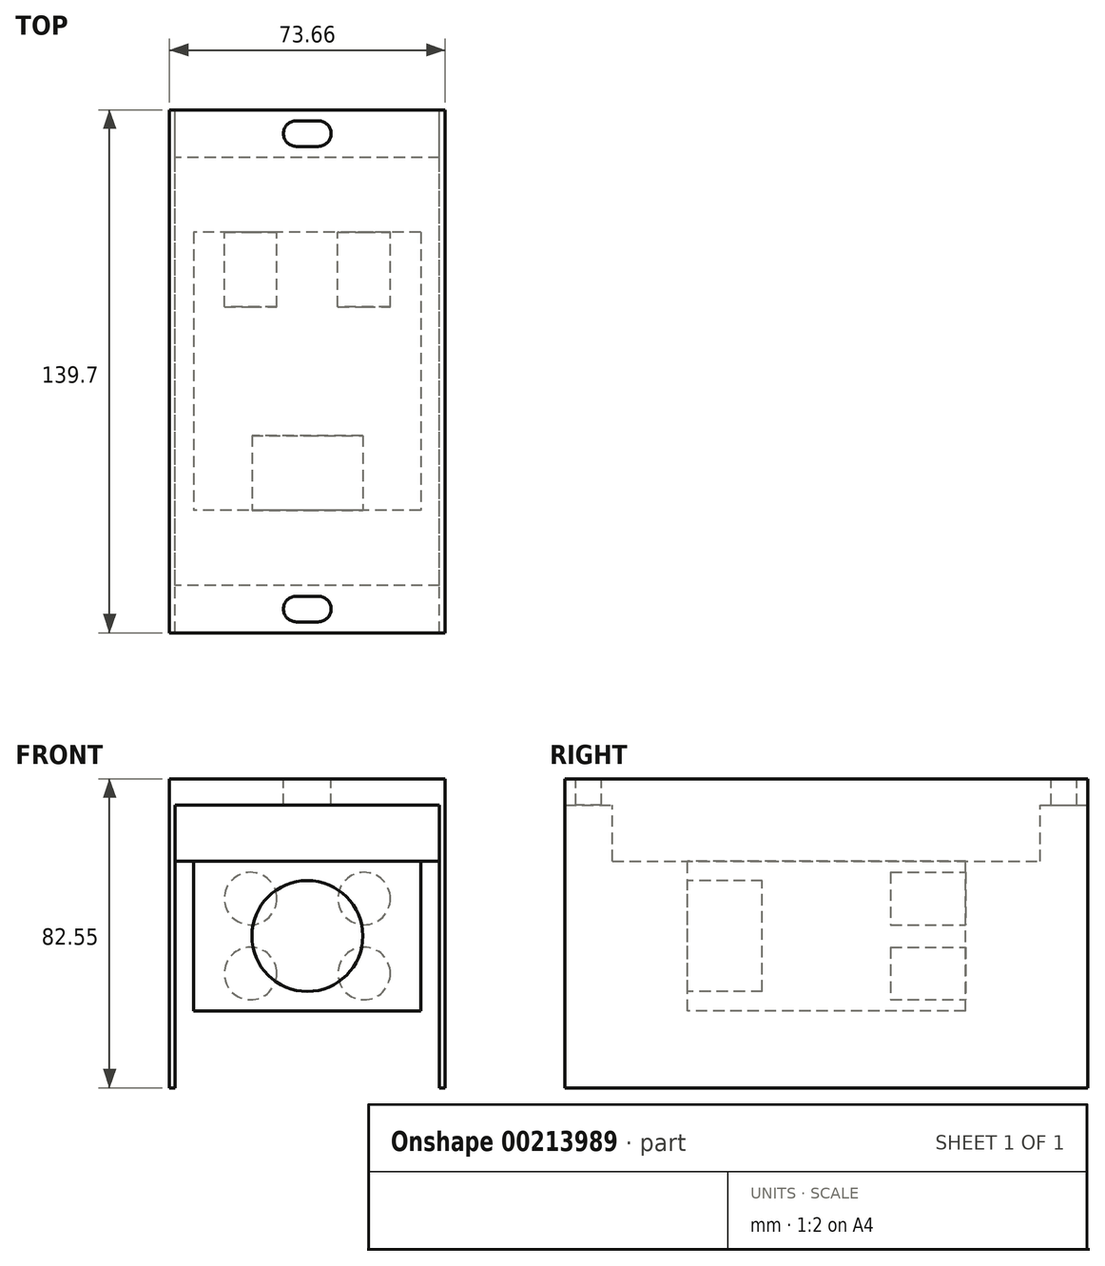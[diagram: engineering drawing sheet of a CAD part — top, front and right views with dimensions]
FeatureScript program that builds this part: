
annotation { "Feature Type Name" : "Feature", "Feature Type Description" : "" }
export const myFeature = defineFeature(function(context is Context, id is Id, definition is map)
    precondition{}
    {
        {
            var Q0;
            Q0=qCreatedBy(makeId("Top.planeOp"),FACE);
            var sketch = newSketch(context, id + "F0", { "sketchPlane" : qUnion([Q0])});
            skLineSegment(sketch, "E0.bottom", {"start": v(-36.83, 69.85) * mm, "end": v(36.83, 69.85) * mm});
            skLineSegment(sketch, "E0.top", {"start": v(-36.83, -69.85) * mm, "end": v(36.83, -69.85) * mm});
            skLineSegment(sketch, "E0.left", {"start": v(-36.83, 69.85) * mm, "end": v(-36.83, -69.85) * mm});
            skLineSegment(sketch, "E0.right", {"start": v(36.83, 69.85) * mm, "end": v(36.83, -69.85) * mm});
            skPoint(sketch, "E0.middle", {"position": v(0, 0) * mm});
            skCircle(sketch, "E1", {"center": v(2.92, 63.5) * mm, "radius": 3.43 * mm});
            skCircle(sketch, "E2", {"center": v(-2.92, 63.5) * mm, "radius": 3.43 * mm});
            skLineSegment(sketch, "E3", {"start": v(0, 69.85) * mm, "end": v(0, -69.85) * mm, "construction": true});
            skLineSegment(sketch, "E4", {"start": v(2.92, 66.93) * mm, "end": v(-2.92, 66.93) * mm});
            skLineSegment(sketch, "E5", {"start": v(-2.92, 60.07) * mm, "end": v(2.92, 60.07) * mm});
            skLineSegment(sketch, "E6", {"start": v(36.83, 0) * mm, "end": v(-36.83, 0) * mm, "construction": true});
            skLineSegment(sketch, "E7.MirrorCS", {"start": v(-2.92, -60.07) * mm, "end": v(2.92, -60.07) * mm});
            skCircle(sketch, "E8.MirrorC", {"center": v(-2.92, -63.5) * mm, "radius": 3.43 * mm});
            skLineSegment(sketch, "E9.MirrorCS", {"start": v(2.92, -66.93) * mm, "end": v(-2.92, -66.93) * mm});
            skCircle(sketch, "E10.MirrorC", {"center": v(2.92, -63.5) * mm, "radius": 3.43 * mm});
            skLineSegment(sketch, "E11", {"start": v(35.33, -69.85) * mm, "end": v(35.33, 69.85) * mm});
            skLineSegment(sketch, "E12.MirrorCS", {"start": v(-35.33, -69.85) * mm, "end": v(-35.33, 69.85) * mm});
            skLineSegment(sketch, "E13", {"start": v(35.33, 57.15) * mm, "end": v(-35.33, 57.15) * mm});
            skLineSegment(sketch, "E14.MirrorCS", {"start": v(35.33, -57.15) * mm, "end": v(-35.33, -57.15) * mm});
            skLineSegment(sketch, "E15", {"start": v(0, 57.15) * mm, "end": v(0, 69.85) * mm, "construction": true});
            skPoint(sketch, "E16", {"position": v(0, 63.5) * mm});
            skSolve(sketch);
        }
        {
            var Q0;
            {var subQ0=sQuery(id+"F0.wireOp",EDGE,"E13");Q0=makeQuery(id+"F0.imprint","IMPRINT",FACE,{"disambiguationData":[TD([[makeQuery(id+"F0.imprint","IMPRINT",EDGE,{"derivedFrom":subQ0}),1.0]])]});}
            extrude(context, id + "F1", {"entities" : qUnion([Q0]), "oppositeDirection" : true, "depth" : 22 * mm});
        }
        {
            var Q0;
            {var subQ2=sQuery(id+"F0.wireOp",EDGE,"E7.MirrorCS");Q0=makeQuery(id+"F0.imprint","IMPRINT",FACE,{"disambiguationData":[TD([[makeQuery(id+"F0.imprint","IMPRINT",EDGE,{"derivedFrom":subQ2}),1.0]])]});}
            var Q1;
            {var subQ0=sQuery(id+"F0.wireOp",EDGE,"E4");Q1=makeQuery(id+"F0.imprint","IMPRINT",FACE,{"disambiguationData":[TD([[makeQuery(id+"F0.imprint","IMPRINT",EDGE,{"derivedFrom":subQ0}),-1.0]])]});}
            extrude(context, id + "F2", {"entities" : qUnion([Q0, Q1]), "operationType" : NewBodyOperationType.ADD, "oppositeDirection" : true, "depth" : 7 * mm});
        }
        {
            var Q0;
            {var subQ0=sQuery(id+"F0.wireOp",EDGE,"E0.left");Q0=makeQuery(id+"F0.imprint","IMPRINT",FACE,{"disambiguationData":[TD([[makeQuery(id+"F0.imprint","IMPRINT",EDGE,{"derivedFrom":subQ0}),1.0]])]});}
            var Q1;
            {var subQ0=sQuery(id+"F0.wireOp",EDGE,"E0.right");Q1=makeQuery(id+"F0.imprint","IMPRINT",FACE,{"disambiguationData":[TD([[makeQuery(id+"F0.imprint","IMPRINT",EDGE,{"derivedFrom":subQ0}),-1.0]])]});}
            extrude(context, id + "F3", {"entities" : qUnion([Q0, Q1]), "operationType" : NewBodyOperationType.ADD, "oppositeDirection" : true, "depth" : 82.55 * mm});
        }
        {
            var Q0;
            Q0=makeQuery(id+"F1.opExtrude","CAP_FACE",FACE,{"disambiguationData":[OSD([sQuery(id+"F0.wireOp",EDGE,"E11"),sQuery(id+"F0.wireOp",EDGE,"E12.MirrorCS"),sQuery(id+"F0.wireOp",EDGE,"E13"),sQuery(id+"F0.wireOp",EDGE,"E14.MirrorCS")])],"isStart":false});
            var sketch = newSketch(context, id + "F4", { "sketchPlane" : qUnion([Q0])});
            skLineSegment(sketch, "E17.bottom", {"start": v(30.33, -37.15) * mm, "end": v(-30.33, -37.15) * mm});
            skLineSegment(sketch, "E17.top", {"start": v(30.33, 37.15) * mm, "end": v(-30.33, 37.15) * mm});
            skLineSegment(sketch, "E17.left", {"start": v(30.33, -37.15) * mm, "end": v(30.33, 37.15) * mm});
            skLineSegment(sketch, "E17.right", {"start": v(-30.33, -37.15) * mm, "end": v(-30.33, 37.15) * mm});
            skSolve(sketch);
        }
        {
            var Q0;
            Q0=makeQuery(id+"F4.imprint","IMPRINT",FACE,{"disambiguationData":[TD([[makeQuery(id+"F4.imprint","IMPRINT",EDGE,{"derivedFrom":sQuery(id+"F4.wireOp",EDGE,"E17.bottom")}),-1.0]])]});
            extrude(context, id + "F5", {"entities" : qUnion([Q0]), "operationType" : NewBodyOperationType.ADD, "depth" : 40 * mm});
        }
        {
            var Q0;
            Q0=makeQuery(id+"F5.opExtrude","SWEPT_FACE",FACE,{"disambiguationData":[OSD([sQuery(id+"F4.wireOp",EDGE,"E17.top")])]});
            var sketch = newSketch(context, id + "F6", { "sketchPlane" : qUnion([Q0])});
            skCircle(sketch, "E18", {"center": v(0, -42) * mm, "radius": 14.82 * mm});
            skPoint(sketch, "E18.centerSnap0", {"position": v(-30.33, -42) * mm});
            skPoint(sketch, "E18.centerSnap1", {"position": v(0, -62) * mm});
            skSolve(sketch);
        }
        {
            var Q0;
            Q0=makeQuery(id+"F6.imprint","IMPRINT",FACE,{"disambiguationData":[TD([[makeQuery(id+"F6.imprint","IMPRINT",EDGE,{"derivedFrom":sQuery(id+"F6.wireOp",EDGE,"E18")}),1.0]])]});
            extrude(context, id + "F7", {"entities" : qUnion([Q0]), "operationType" : NewBodyOperationType.REMOVE, "oppositeDirection" : true, "depth" : 20 * mm});
        }
        {
            var Q0;
            Q0=makeQuery(id+"F5.opExtrude","SWEPT_FACE",FACE,{"disambiguationData":[OSD([sQuery(id+"F4.wireOp",EDGE,"E17.bottom")])]});
            var sketch = newSketch(context, id + "F8", { "sketchPlane" : qUnion([Q0])});
            skLineSegment(sketch, "E19", {"start": v(0, -62) * mm, "end": v(0, -42) * mm, "construction": true});
            skLineSegment(sketch, "E20", {"start": v(0, -42) * mm, "end": v(0, -22) * mm, "construction": true});
            skLineSegment(sketch, "E21", {"start": v(0, -42) * mm, "end": v(30.33, -42) * mm, "construction": true});
            skLineSegment(sketch, "E22", {"start": v(0, -42) * mm, "end": v(-30.33, -42) * mm, "construction": true});
            skCircle(sketch, "E23", {"center": v(15.17, -52) * mm, "radius": 7 * mm});
            skPoint(sketch, "E23.centerSnap0", {"position": v(0, -52) * mm});
            skPoint(sketch, "E23.centerSnap1", {"position": v(15.17, -42) * mm});
            skCircle(sketch, "E24", {"center": v(-15.17, -52) * mm, "radius": 7 * mm});
            skPoint(sketch, "E24.centerSnap0", {"position": v(-15.17, -42) * mm});
            skCircle(sketch, "E25", {"center": v(-15.17, -32) * mm, "radius": 7 * mm});
            skPoint(sketch, "E25.centerSnap0", {"position": v(0, -32) * mm});
            skCircle(sketch, "E26", {"center": v(15.17, -32) * mm, "radius": 7 * mm});
            skSolve(sketch);
        }
        {
            var Q0;
            Q0=makeQuery(id+"F8.imprint","IMPRINT",FACE,{"disambiguationData":[TD([[makeQuery(id+"F8.imprint","IMPRINT",EDGE,{"derivedFrom":sQuery(id+"F8.wireOp",EDGE,"E26")}),1.0]])]});
            var Q1;
            Q1=makeQuery(id+"F8.imprint","IMPRINT",FACE,{"disambiguationData":[TD([[makeQuery(id+"F8.imprint","IMPRINT",EDGE,{"derivedFrom":sQuery(id+"F8.wireOp",EDGE,"E23")}),1.0]])]});
            var Q2;
            Q2=makeQuery(id+"F8.imprint","IMPRINT",FACE,{"disambiguationData":[TD([[makeQuery(id+"F8.imprint","IMPRINT",EDGE,{"derivedFrom":sQuery(id+"F8.wireOp",EDGE,"E24")}),1.0]])]});
            var Q3;
            Q3=makeQuery(id+"F8.imprint","IMPRINT",FACE,{"disambiguationData":[TD([[makeQuery(id+"F8.imprint","IMPRINT",EDGE,{"derivedFrom":sQuery(id+"F8.wireOp",EDGE,"E25")}),1.0]])]});
            var Q4;
            Q4=sQuery(id+"F8.wireOp",EDGE,"E24");
            extrude(context, id + "F9", {"entities" : qUnion([Q0, Q1, Q2, Q3]), "operationType" : NewBodyOperationType.REMOVE, "surfaceEntities" : qUnion([Q4]), "oppositeDirection" : true, "depth" : 20 * mm});
        }
    });
